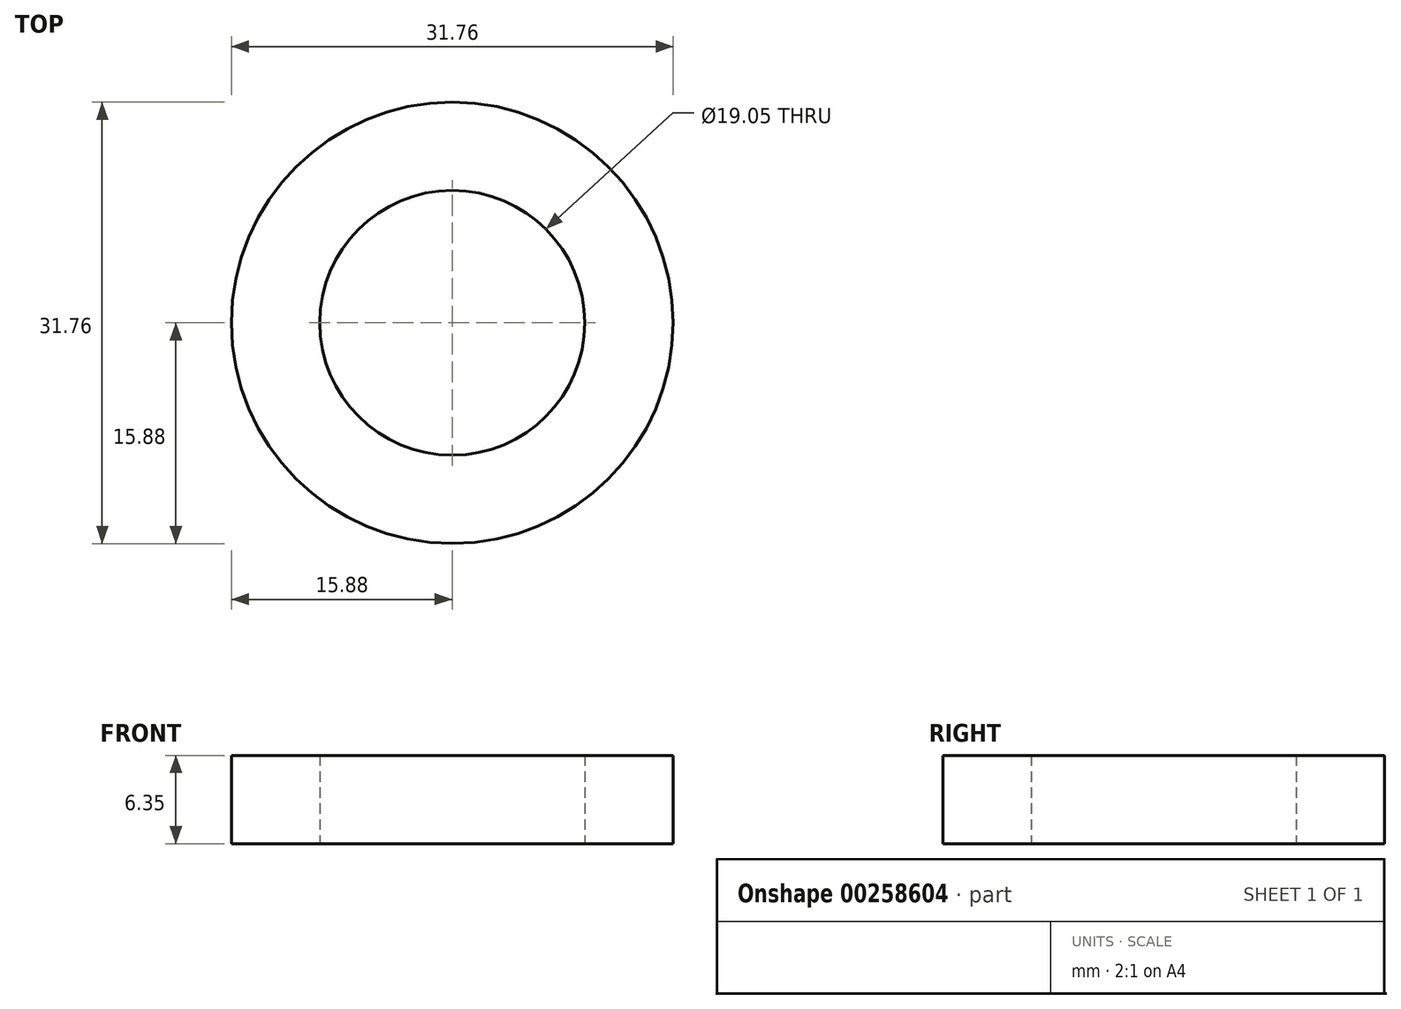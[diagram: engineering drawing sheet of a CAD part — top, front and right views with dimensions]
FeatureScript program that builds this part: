
annotation { "Feature Type Name" : "Feature", "Feature Type Description" : "" }
export const myFeature = defineFeature(function(context is Context, id is Id, definition is map)
    precondition{}
    {
        {
            var Q0;
            Q0=qCreatedBy(makeId("Top.planeOp"),FACE);
            var sketch = newSketch(context, id + "F0", { "sketchPlane" : qUnion([Q0])});
            skCircle(sketch, "E0", {"center": v(0, 0) * mm, "radius": 15.88 * mm});
            skCircle(sketch, "E1", {"center": v(0, 0) * mm, "radius": 9.53 * mm});
            skSolve(sketch);
        }
        {
            var Q0;
            Q0 = qSketchRegion(id + "F0", true);
            extrude(context, id + "F1", {"entities" : qUnion([Q0]), "depth" : 6.35 * mm});
        }
    });
